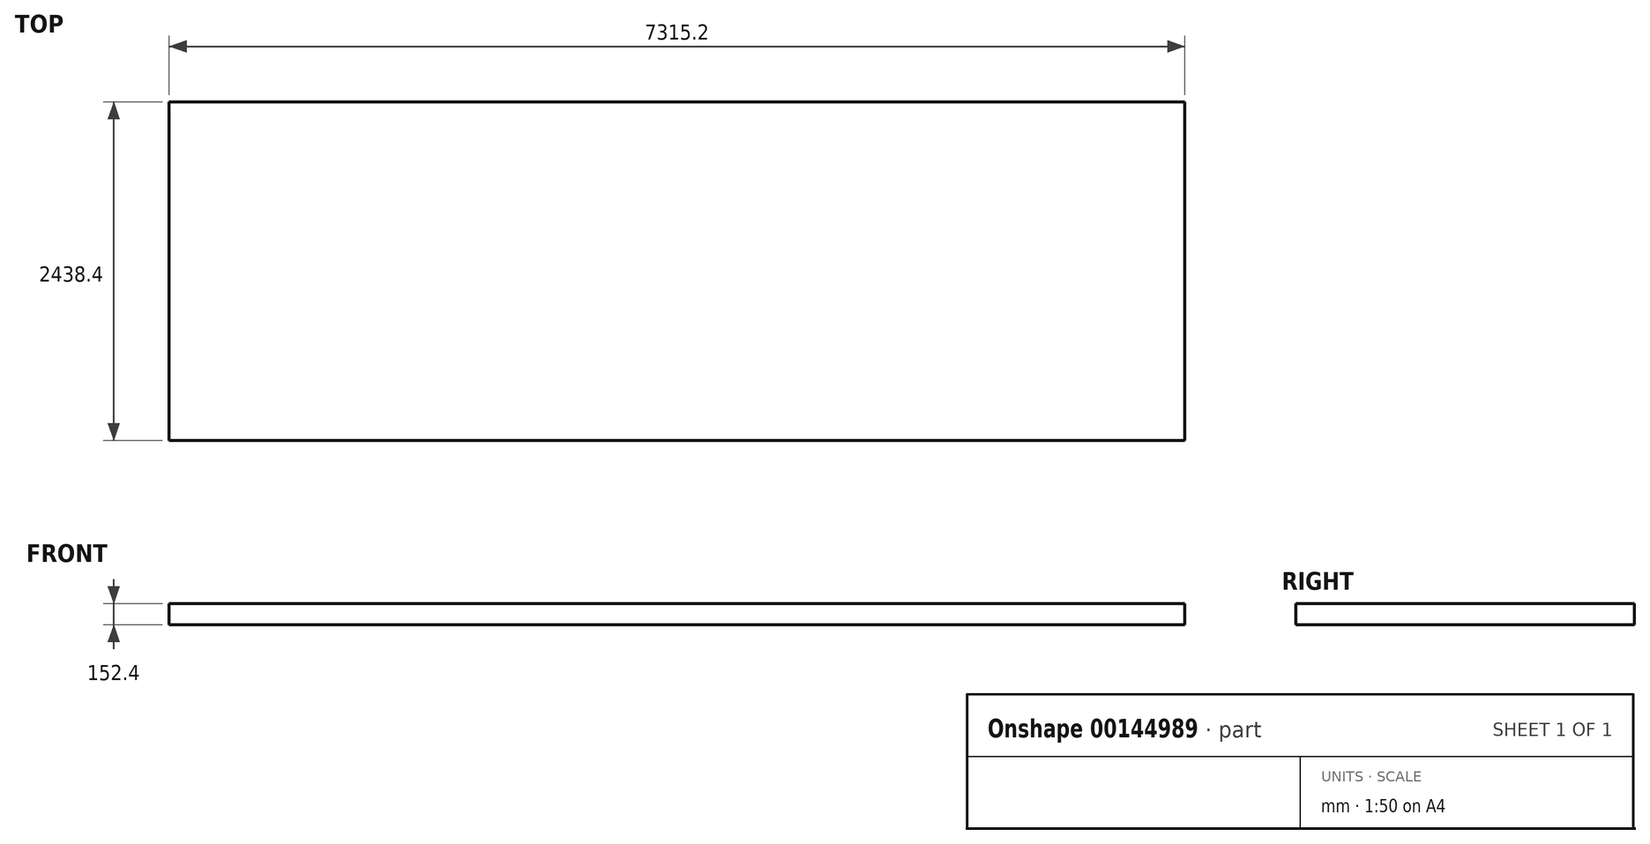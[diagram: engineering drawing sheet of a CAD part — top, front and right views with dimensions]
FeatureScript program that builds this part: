
annotation { "Feature Type Name" : "Feature", "Feature Type Description" : "" }
export const myFeature = defineFeature(function(context is Context, id is Id, definition is map)
    precondition{}
    {
        {
            var Q0;
            Q0=qCreatedBy(makeId("Front.planeOp"),FACE);
            var sketch = newSketch(context, id + "F0", { "sketchPlane" : qUnion([Q0])});
            skLineSegment(sketch, "E0.bottom", {"start": v(0, 0) * mm, "end": v(7315.2, 0) * mm});
            skLineSegment(sketch, "E0.top", {"start": v(0, 152.4) * mm, "end": v(7315.2, 152.4) * mm});
            skLineSegment(sketch, "E0.left", {"start": v(0, 0) * mm, "end": v(0, 152.4) * mm});
            skLineSegment(sketch, "E0.right", {"start": v(7315.2, 0) * mm, "end": v(7315.2, 152.4) * mm});
            skSolve(sketch);
        }
        {
            var Q0;
            Q0 = qSketchRegion(id + "F0", true);
            extrude(context, id + "F1", {"entities" : qUnion([Q0]), "oppositeDirection" : true, "depth" : 2438.4 * mm});
        }
    });
